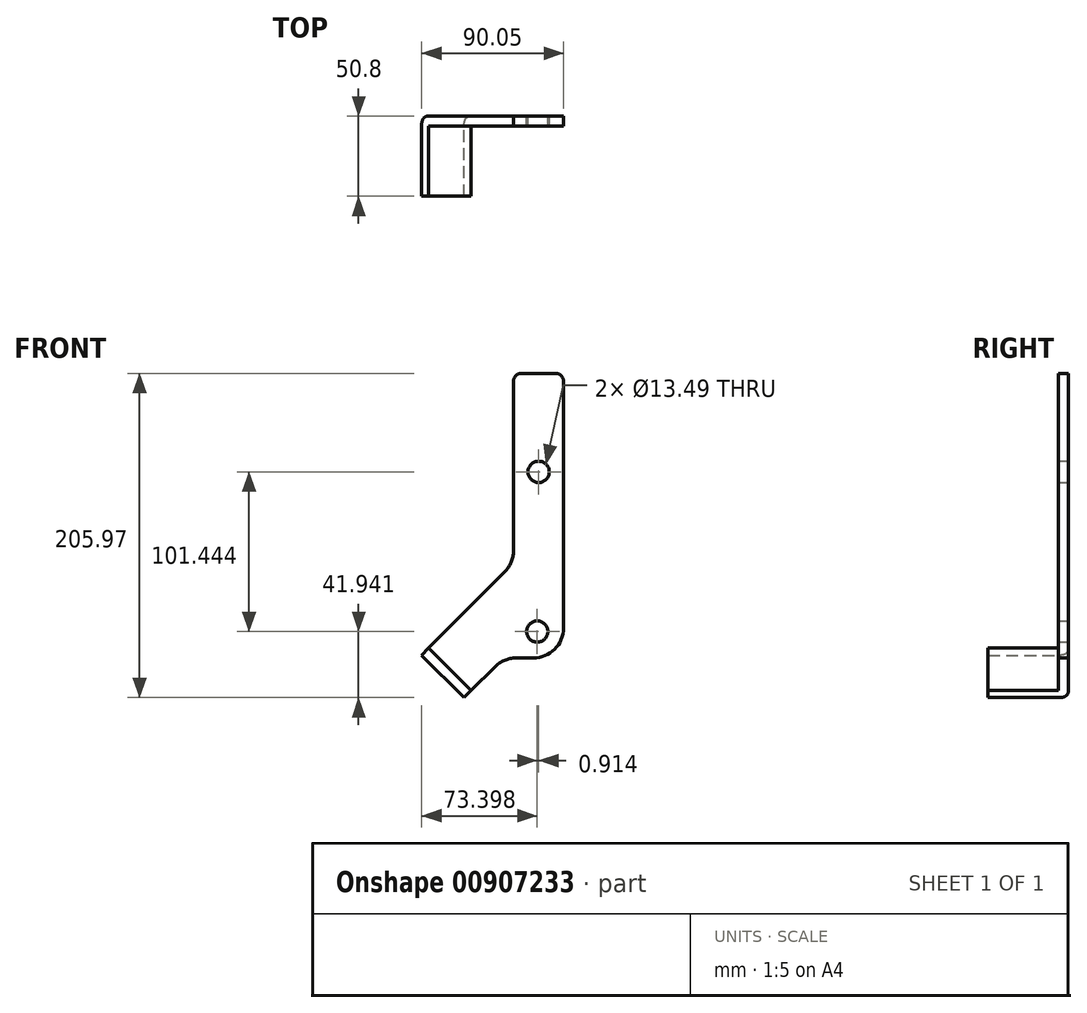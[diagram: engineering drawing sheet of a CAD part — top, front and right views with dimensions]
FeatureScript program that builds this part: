
annotation { "Feature Type Name" : "Feature", "Feature Type Description" : "" }
export const myFeature = defineFeature(function(context is Context, id is Id, definition is map)
    precondition{}
    {
        {
            var Q0;
            Q0=qCreatedBy(makeId("Front.planeOp"),FACE);
            var sketch = newSketch(context, id + "F0", { "sketchPlane" : qUnion([Q0])});
            skLineSegment(sketch, "E0", {"start": v(6.25, 180.83) * mm, "end": v(38, 180.83) * mm});
            skLineSegment(sketch, "E1", {"start": v(38, 180.83) * mm, "end": v(38, 33.02) * mm});
            skLineSegment(sketch, "E2", {"start": v(6.25, 60.22) * mm, "end": v(6.25, 180.83) * mm});
            skLineSegment(sketch, "E3", {"start": v(0, 0) * mm, "end": v(-20.58, -20.64) * mm});
            skLineSegment(sketch, "E4", {"start": v(-20.58, -20.64) * mm, "end": v(-47.56, 6.27) * mm});
            skLineSegment(sketch, "E5", {"start": v(-47.56, 6.27) * mm, "end": v(6.25, 60.22) * mm});
            skLineSegment(sketch, "E6", {"start": v(6.25, 0) * mm, "end": v(38, 0) * mm});
            skLineSegment(sketch, "E7", {"start": v(38, 0) * mm, "end": v(38, 33.02) * mm});
            skLineSegment(sketch, "E8", {"start": v(38, 0) * mm, "end": v(0, 0) * mm});
            skPoint(sketch, "E9.orphan", {"position": v(0, 0) * mm});
            skSolve(sketch);
        }
        {
            var Q0;
            Q0 = qSketchRegion(id + "F0", true);
            extrude(context, id + "F1", {"entities" : qUnion([Q0]), "depth" : 6.35 * mm, "offsetDistance" : 25.4 * mm});
        }
        {
            var Q0;
            Q0=makeQuery(id+"F1.opExtrude","CAP_FACE",FACE,{"disambiguationData":[OSD([sQuery(id+"F0.wireOp",EDGE,"E0"),sQuery(id+"F0.wireOp",EDGE,"E1"),sQuery(id+"F0.wireOp",EDGE,"E2"),sQuery(id+"F0.wireOp",EDGE,"E3"),sQuery(id+"F0.wireOp",EDGE,"E4"),sQuery(id+"F0.wireOp",EDGE,"E5"),sQuery(id+"F0.wireOp",EDGE,"gKiY4kpW-ng0u-sDTf-hIyV-E0I1T0kX8aFS")])],"isStart":true});
            var sketch = newSketch(context, id + "F2", { "sketchPlane" : qUnion([Q0])});
            skLineSegment(sketch, "E10", {"start": v(47.56, 6.27) * mm, "end": v(52.05, 1.77) * mm});
            skLineSegment(sketch, "E11", {"start": v(25.07, -25.14) * mm, "end": v(52.05, 1.77) * mm});
            skLineSegment(sketch, "E12", {"start": v(25.07, -25.14) * mm, "end": v(20.58, -20.64) * mm});
            skLineSegment(sketch, "E13", {"start": v(47.56, 6.27) * mm, "end": v(20.58, -20.64) * mm});
            skSolve(sketch);
        }
        {
            var Q0;
            Q0 = qSketchRegion(id + "F2", true);
            extrude(context, id + "F3", {"entities" : qUnion([Q0]), "operationType" : NewBodyOperationType.ADD, "oppositeDirection" : true, "depth" : 50.8 * mm, "offsetDistance" : 25.4 * mm});
        }
        {
            var Q0;
            Q0=makeQuery(id+"F1.opExtrude","CAP_FACE",FACE,{"disambiguationData":[OSD([sQuery(id+"F0.wireOp",EDGE,"E0"),sQuery(id+"F0.wireOp",EDGE,"E1"),sQuery(id+"F0.wireOp",EDGE,"E2"),sQuery(id+"F0.wireOp",EDGE,"E3"),sQuery(id+"F0.wireOp",EDGE,"E4"),sQuery(id+"F0.wireOp",EDGE,"E5"),sQuery(id+"F0.wireOp",EDGE,"gKiY4kpW-ng0u-sDTf-hIyV-E0I1T0kX8aFS")])],"isStart":false});
            var sketch = newSketch(context, id + "F4", { "sketchPlane" : qUnion([Q0])});
            skPoint(sketch, "E14", {"position": v(22.26, 118.24) * mm});
            skPoint(sketch, "E15", {"position": v(21.35, 16.8) * mm});
            skCircle(sketch, "E16", {"center": v(22.26, 118.24) * mm, "radius": 7.2 * mm, "construction": true});
            skCircle(sketch, "E17", {"center": v(21.35, 16.8) * mm, "radius": 7.2 * mm, "construction": true});
            skSolve(sketch);
        }
        {
            var Q0;
            Q0=sQuery(id+"F4.wireOp",VERTEX,"E14");
            var Q1;
            Q1=sQuery(id+"F4.wireOp",VERTEX,"E15");
            var Q2;
            Q2=makeQuery(id+"F1.opExtrude","SWEPT_BODY",BODY,{"disambiguationData":[OSD([sQuery(id+"F0.wireOp",EDGE,"E0"),sQuery(id+"F0.wireOp",EDGE,"E1"),sQuery(id+"F0.wireOp",EDGE,"E2"),sQuery(id+"F0.wireOp",EDGE,"E3"),sQuery(id+"F0.wireOp",EDGE,"E4"),sQuery(id+"F0.wireOp",EDGE,"E5"),sQuery(id+"F0.wireOp",EDGE,"gKiY4kpW-ng0u-sDTf-hIyV-E0I1T0kX8aFS")])]});
            hole(context, id + "F5", {"style" : HoleStyle.SIMPLE, "endStyle" : HoleEndStyle.THROUGH, "standardTappedOrClearance" : lookupTablePath({ "fit" : "Free", "standard" : "ANSI", "size" : "1/2", "type" : "Clearance" }), "standardBlindInLast" : lookupTablePath({ "fit" : "Free", "standard" : "ANSI", "engagement" : "75%", "pitch" : "13 tpi", "size" : "1/2", "type" : "Clearance & tapped" }), "holeDiameter" : 13.5 * mm, "majorDiameter" : 12.7 * mm, "isTappedThrough" : true, "tappedDepth" : 8.47 * mm, "tapClearance" : 3, "locations" : qUnion([Q0, Q1]), "scope" : qUnion([Q2]), "startStyle" : HoleStartStyle.SKETCH});
        }
        {
            var Q0;
            Q0=makeQuery(id+"F1.opExtrude","SWEPT_EDGE",EDGE,{"disambiguationData":[OSD([sQuery(id+"F0.wireOp",EDGE,"E2"),sQuery(id+"F0.wireOp",EDGE,"E5")])]});
            var Q1;
            Q1=makeQuery(id+"F1.opExtrude","SWEPT_EDGE",EDGE,{"disambiguationData":[OSD([sQuery(id+"F0.wireOp",EDGE,"E7"),sQuery(id+"F0.wireOp",EDGE,"E8")])]});
            var Q2;
            Q2=makeQuery(id+"F1.opExtrude","SWEPT_EDGE",EDGE,{"disambiguationData":[OSD([sQuery(id+"F0.wireOp",EDGE,"E3"),sQuery(id+"F0.wireOp",EDGE,"E8")])]});
            fillet(context, id + "F6", {"entities" : qUnion([Q0, Q1, Q2]), "tangentPropagation" : true, "radius" : 19.05 * mm, "defaultsChanged" : false, "vertexSettings" : [], "allowEdgeOverflow" : false});
        }
        {
            var Q0;
            Q0=makeQuery(id+"F3.opExtrude","CAP_EDGE",EDGE,{"disambiguationData":[OSD([sQuery(id+"F2.wireOp",EDGE,"E11")])],"isStart":true});
            var Q1;
            Q1=makeQuery(id+"F1.opExtrude","CAP_EDGE",EDGE,{"disambiguationData":[OSD([sQuery(id+"F0.wireOp",EDGE,"E4")])],"isStart":false});
            fillet(context, id + "F7", {"entities" : qUnion([Q0, Q1]), "tangentPropagation" : true, "radius" : 5.08 * mm, "defaultsChanged" : false, "vertexSettings" : [], "allowEdgeOverflow" : false});
        }
        {
            var Q0;
            Q0=makeQuery(id+"F1.opExtrude","SWEPT_EDGE",EDGE,{"disambiguationData":[OSD([sQuery(id+"F0.wireOp",EDGE,"E0"),sQuery(id+"F0.wireOp",EDGE,"E2")])]});
            var Q1;
            Q1=makeQuery(id+"F1.opExtrude","SWEPT_EDGE",EDGE,{"disambiguationData":[OSD([sQuery(id+"Fq38At4ci81HlFv_0.wireOp",EDGE,"VVe9A18r-VORx-4CNg-MuIO-dTXUSACqtpxO"),sQuery(id+"F0.wireOp",EDGE,"E0"),sQuery(id+"F0.wireOp",EDGE,"E1")])]});
            fillet(context, id + "F8", {"entities" : qUnion([Q0, Q1]), "tangentPropagation" : true, "radius" : 5.08 * mm, "defaultsChanged" : false, "vertexSettings" : [], "allowEdgeOverflow" : false});
        }
    });
